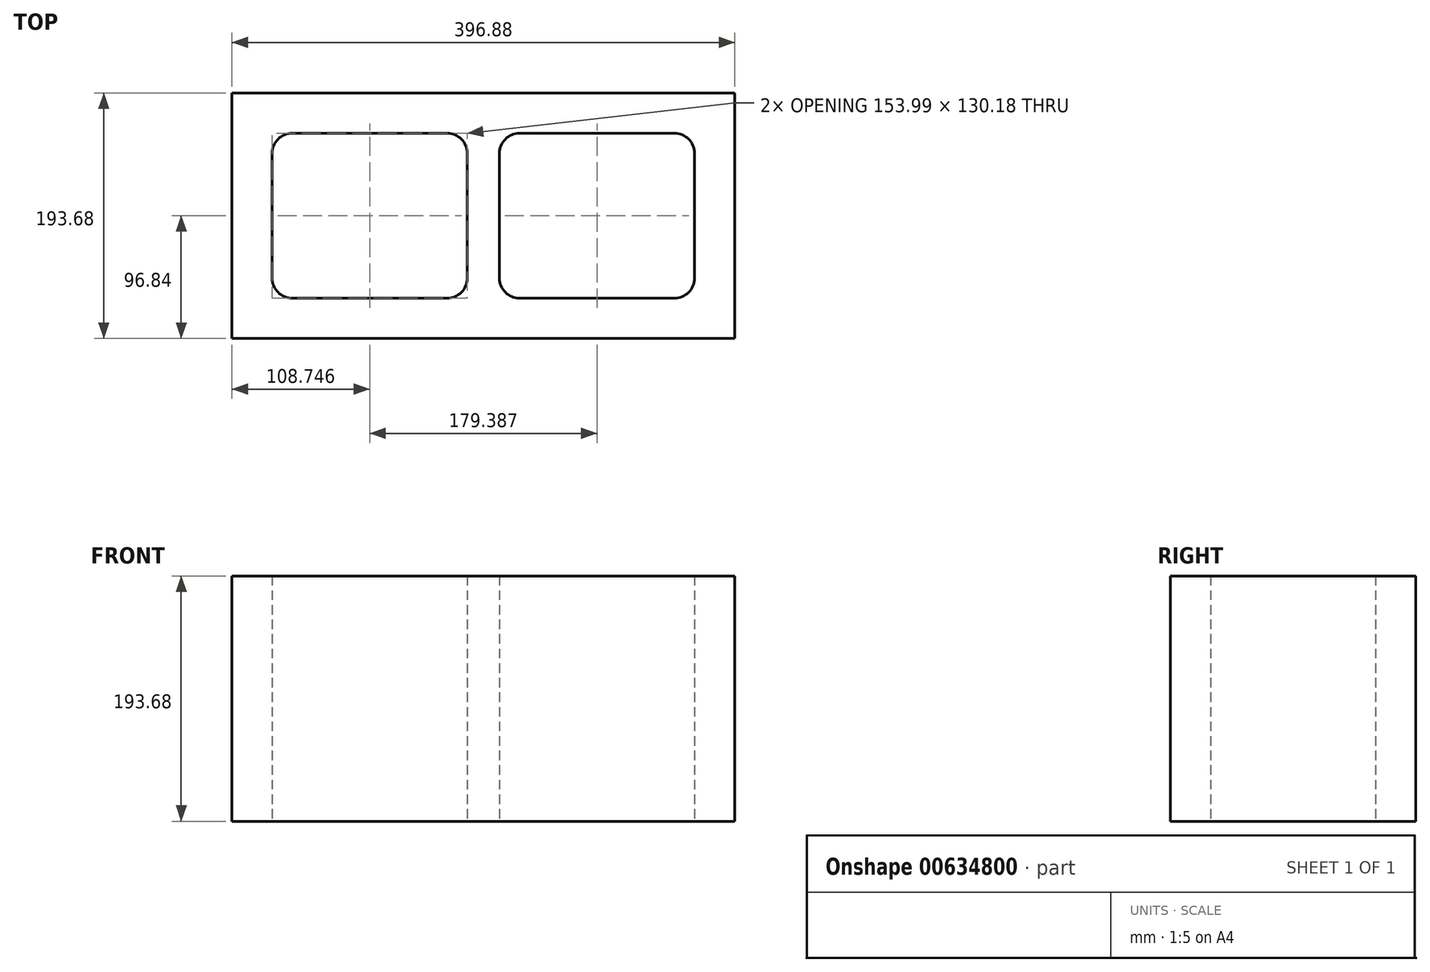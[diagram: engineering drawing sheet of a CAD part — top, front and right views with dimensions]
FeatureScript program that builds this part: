
annotation { "Feature Type Name" : "Feature", "Feature Type Description" : "" }
export const myFeature = defineFeature(function(context is Context, id is Id, definition is map)
    precondition{}
    {
        {
            var Q0;
            Q0=qCreatedBy(makeId("Top.planeOp"),FACE);
            var sketch = newSketch(context, id + "F0", { "sketchPlane" : qUnion([Q0])});
            skLineSegment(sketch, "E0.bottom", {"start": v(-198.44, 96.84) * mm, "end": v(198.44, 96.84) * mm});
            skLineSegment(sketch, "E0.top", {"start": v(-198.44, -96.84) * mm, "end": v(198.44, -96.84) * mm});
            skLineSegment(sketch, "E0.left", {"start": v(-198.44, 96.84) * mm, "end": v(-198.44, -96.84) * mm});
            skLineSegment(sketch, "E0.right", {"start": v(198.44, 96.84) * mm, "end": v(198.44, -96.84) * mm});
            skLineSegment(sketch, "E1.bottom", {"start": v(-150.81, 65.09) * mm, "end": v(-28.57, 65.09) * mm});
            skLineSegment(sketch, "E1.top", {"start": v(-150.81, -65.09) * mm, "end": v(-28.58, -65.09) * mm});
            skLineSegment(sketch, "E1.left", {"start": v(-166.69, 49.21) * mm, "end": v(-166.69, -49.21) * mm});
            skLineSegment(sketch, "E1.right", {"start": v(-12.7, 49.21) * mm, "end": v(-12.7, -49.21) * mm});
            skLineSegment(sketch, "E2", {"start": v(0, 96.84) * mm, "end": v(0, -96.84) * mm, "construction": true});
            skLineSegment(sketch, "E3.MirrorCS", {"start": v(166.69, 49.21) * mm, "end": v(166.69, -49.21) * mm});
            skLineSegment(sketch, "E4.MirrorCS", {"start": v(150.81, 65.09) * mm, "end": v(28.57, 65.09) * mm});
            skLineSegment(sketch, "E5.MirrorCS", {"start": v(150.81, -65.09) * mm, "end": v(28.57, -65.09) * mm});
            skLineSegment(sketch, "E6.MirrorCS", {"start": v(12.7, 49.21) * mm, "end": v(12.7, -49.21) * mm});
            skPoint(sketch, "E7.visualSharp", {"position": v(-166.69, 65.09) * mm});
            skArc(sketch, "E7.filletArc", {"start": v(-150.81, 65.09) * mm, "mid": v(-162.04, 60.44) * mm, "end": v(-166.69, 49.21) * mm});
            skPoint(sketch, "E8.visualSharp", {"position": v(-166.69, -65.09) * mm});
            skArc(sketch, "E8.filletArc", {"start": v(-166.69, -49.21) * mm, "mid": v(-162.04, -60.44) * mm, "end": v(-150.81, -65.09) * mm});
            skPoint(sketch, "E9.visualSharp", {"position": v(-12.7, -65.09) * mm});
            skArc(sketch, "E9.filletArc", {"start": v(-28.58, -65.09) * mm, "mid": v(-17.35, -60.44) * mm, "end": v(-12.7, -49.21) * mm});
            skPoint(sketch, "E10.visualSharp", {"position": v(-12.7, 65.09) * mm});
            skArc(sketch, "E10.filletArc", {"start": v(-12.7, 49.21) * mm, "mid": v(-17.35, 60.44) * mm, "end": v(-28.57, 65.09) * mm});
            skPoint(sketch, "E11.visualSharp", {"position": v(12.7, 65.09) * mm});
            skArc(sketch, "E11.filletArc", {"start": v(28.57, 65.09) * mm, "mid": v(17.35, 60.44) * mm, "end": v(12.7, 49.21) * mm});
            skPoint(sketch, "E12.visualSharp", {"position": v(12.7, -65.09) * mm});
            skArc(sketch, "E12.filletArc", {"start": v(12.7, -49.21) * mm, "mid": v(17.35, -60.44) * mm, "end": v(28.57, -65.09) * mm});
            skPoint(sketch, "E13.visualSharp", {"position": v(166.69, -65.09) * mm});
            skArc(sketch, "E13.filletArc", {"start": v(150.81, -65.09) * mm, "mid": v(162.04, -60.44) * mm, "end": v(166.69, -49.21) * mm});
            skPoint(sketch, "E14.visualSharp", {"position": v(166.69, 65.09) * mm});
            skArc(sketch, "E14.filletArc", {"start": v(166.69, 49.21) * mm, "mid": v(162.04, 60.44) * mm, "end": v(150.81, 65.09) * mm});
            skLineSegment(sketch, "E15", {"start": v(-12.7, 0) * mm, "end": v(12.7, 0) * mm});
            skSolve(sketch);
        }
        {
            var Q0;
            Q0=makeQuery(id+"F0.imprint","IMPRINT",FACE,{"disambiguationData":[TD([[makeQuery(id+"F0.imprint","IMPRINT",EDGE,{"derivedFrom":sQuery(id+"F0.wireOp",EDGE,"E0.bottom")}),-1.0]])]});
            extrude(context, id + "F1", {"entities" : qUnion([Q0]), "endBound" : BoundingType.SYMMETRIC, "depth" : 193.67 * mm, "offsetDistance" : 25.4 * mm});
        }
    });
